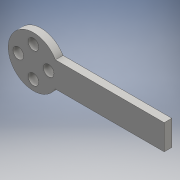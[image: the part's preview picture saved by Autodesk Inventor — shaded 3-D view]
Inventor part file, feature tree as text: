
AUTODESK INVENTOR PART (.ipt)
format: ipt  version: 2016 (Build 200138000, 138)  size: 112,128 bytes
history: native  units: mm
features: extrude x1, sketch x1
ambient origin geometry x8: Origin, YZ Plane, XZ Plane, XY Plane, X Axis, Y Axis, Z Axis, Center Point
bodies: Solid1 (feature_tree)
feature tree (2):
  extrude  "Extrusion1"  Depth=3.0mm
  sketch  "Sketch1"  dims[d0=20.0mm d1=4.25mm d2=6.0mm d3=4.25mm d4=6.0mm d5=4.25mm d6=6.0mm d7=4.25mm d8=6.0mm d9=4.0mm d22=3.0mm d23=0.0mm d26=43.0mm d28=43.0mm]
